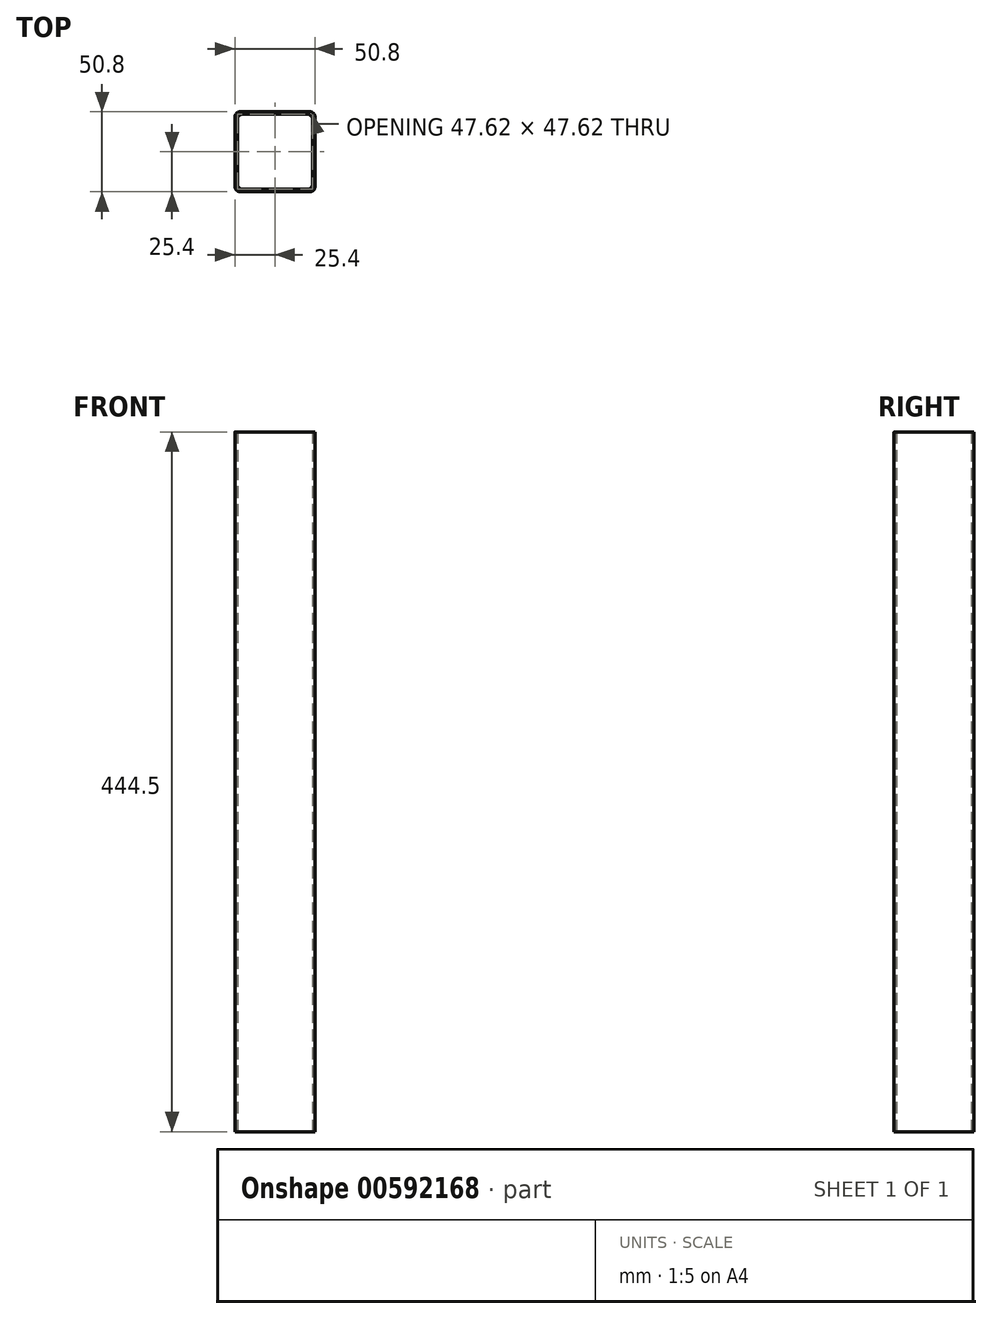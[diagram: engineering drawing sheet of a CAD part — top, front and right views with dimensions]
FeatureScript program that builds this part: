
annotation { "Feature Type Name" : "Feature", "Feature Type Description" : "" }
export const myFeature = defineFeature(function(context is Context, id is Id, definition is map)
    precondition{}
    {
        {
            var Q0;
            Q0=qCreatedBy(makeId("Top.planeOp"),FACE);
            var sketch = newSketch(context, id + "F0", { "sketchPlane" : qUnion([Q0])});
            skLineSegment(sketch, "E0.bottom", {"start": v(22.23, 25.4) * mm, "end": v(-22.23, 25.4) * mm});
            skLineSegment(sketch, "E0.top", {"start": v(22.23, -25.4) * mm, "end": v(-22.23, -25.4) * mm});
            skLineSegment(sketch, "E0.left", {"start": v(25.4, 22.23) * mm, "end": v(25.4, -22.22) * mm});
            skLineSegment(sketch, "E0.right", {"start": v(-25.4, 22.23) * mm, "end": v(-25.4, -22.22) * mm});
            skPoint(sketch, "E0.middle", {"position": v(0, 0) * mm});
            skLineSegment(sketch, "E1.0", {"start": v(20.64, 23.81) * mm, "end": v(-20.64, 23.81) * mm});
            skLineSegment(sketch, "E1.1", {"start": v(23.81, 20.64) * mm, "end": v(23.81, -20.64) * mm});
            skLineSegment(sketch, "E1.2", {"start": v(20.64, -23.81) * mm, "end": v(-20.64, -23.81) * mm});
            skLineSegment(sketch, "E1.3", {"start": v(-23.81, 20.64) * mm, "end": v(-23.81, -20.64) * mm});
            skPoint(sketch, "E2.visualSharp", {"position": v(-23.81, 23.81) * mm});
            skArc(sketch, "E2.filletArc", {"start": v(-20.64, 23.81) * mm, "mid": v(-22.88, 22.88) * mm, "end": v(-23.81, 20.64) * mm});
            skPoint(sketch, "E3.visualSharp", {"position": v(-25.4, 25.4) * mm});
            skArc(sketch, "E3.filletArc", {"start": v(-22.23, 25.4) * mm, "mid": v(-24.47, 24.47) * mm, "end": v(-25.4, 22.23) * mm});
            skPoint(sketch, "E4.visualSharp", {"position": v(23.81, 23.81) * mm});
            skArc(sketch, "E4.filletArc", {"start": v(23.81, 20.64) * mm, "mid": v(22.88, 22.88) * mm, "end": v(20.64, 23.81) * mm});
            skPoint(sketch, "E5.visualSharp", {"position": v(25.4, 25.4) * mm});
            skArc(sketch, "E5.filletArc", {"start": v(25.4, 22.23) * mm, "mid": v(24.47, 24.47) * mm, "end": v(22.23, 25.4) * mm});
            skPoint(sketch, "E6.visualSharp", {"position": v(-23.81, -23.81) * mm});
            skArc(sketch, "E6.filletArc", {"start": v(-23.81, -20.64) * mm, "mid": v(-22.88, -22.88) * mm, "end": v(-20.64, -23.81) * mm});
            skPoint(sketch, "E7.visualSharp", {"position": v(-25.4, -25.4) * mm});
            skArc(sketch, "E7.filletArc", {"start": v(-25.4, -22.22) * mm, "mid": v(-24.47, -24.47) * mm, "end": v(-22.23, -25.4) * mm});
            skPoint(sketch, "E8.visualSharp", {"position": v(23.81, -23.81) * mm});
            skArc(sketch, "E8.filletArc", {"start": v(20.64, -23.81) * mm, "mid": v(22.88, -22.88) * mm, "end": v(23.81, -20.64) * mm});
            skPoint(sketch, "E9.visualSharp", {"position": v(25.4, -25.4) * mm});
            skArc(sketch, "E9.filletArc", {"start": v(22.23, -25.4) * mm, "mid": v(24.47, -24.47) * mm, "end": v(25.4, -22.22) * mm});
            skSolve(sketch);
        }
        {
            var Q0;
            Q0 = qSketchRegion(id + "F0", true);
            extrude(context, id + "F1", {"entities" : qUnion([Q0]), "depth" : 444.5 * mm, "offsetDistance" : 25.4 * mm});
        }
    });
